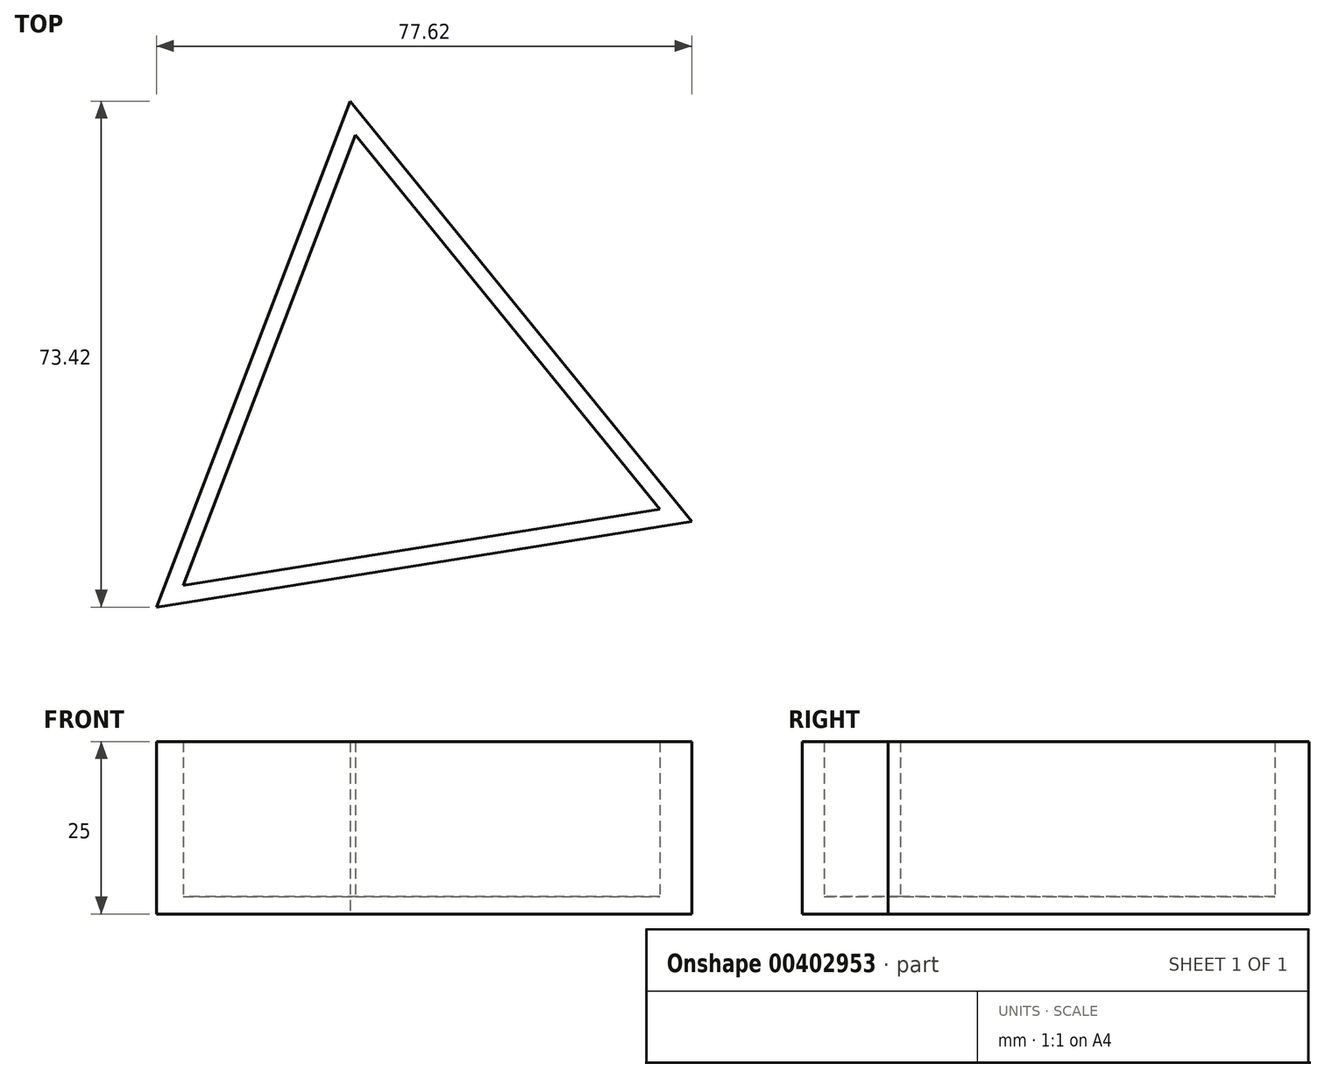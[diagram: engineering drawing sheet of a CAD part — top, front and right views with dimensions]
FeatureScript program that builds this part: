
annotation { "Feature Type Name" : "Feature", "Feature Type Description" : "" }
export const myFeature = defineFeature(function(context is Context, id is Id, definition is map)
    precondition{}
    {
        {
            var Q0;
            Q0=qCreatedBy(makeId("Top.planeOp"),FACE);
            var sketch = newSketch(context, id + "F0", { "sketchPlane" : qUnion([Q0])});
            skCircle(sketch, "E0.cCircle", {"center": v(0, 0) * mm, "radius": 22.7 * mm, "construction": true});
            skLineSegment(sketch, "E0.0", {"start": v(-35.23, -28.6) * mm, "end": v(-7.16, 44.81) * mm});
            skLineSegment(sketch, "E0.1", {"start": v(-7.16, 44.81) * mm, "end": v(42.39, -16.2) * mm});
            skLineSegment(sketch, "E0.2", {"start": v(42.39, -16.2) * mm, "end": v(-35.23, -28.6) * mm});
            skPoint(sketch, "E0.0.midPoint", {"position": v(-21.2, 8.1) * mm});
            skSolve(sketch);
        }
        {
            var Q0;
            Q0 = qSketchRegion(id + "F0", true);
            extrude(context, id + "F1", {"entities" : qUnion([Q0]), "depth" : 25 * mm});
        }
        {
            var Q0;
            Q0=makeQuery(id+"F1.opExtrude","CAP_FACE",FACE,{"disambiguationData":[OSD([sQuery(id+"F0.wireOp",EDGE,"E0.0"),sQuery(id+"F0.wireOp",EDGE,"E0.1"),sQuery(id+"F0.wireOp",EDGE,"E0.2")])],"isStart":false});
            shell(context, id + "F2", {"entities" : qUnion([Q0]), "thickness" : 2.5 * mm});
        }
    });
